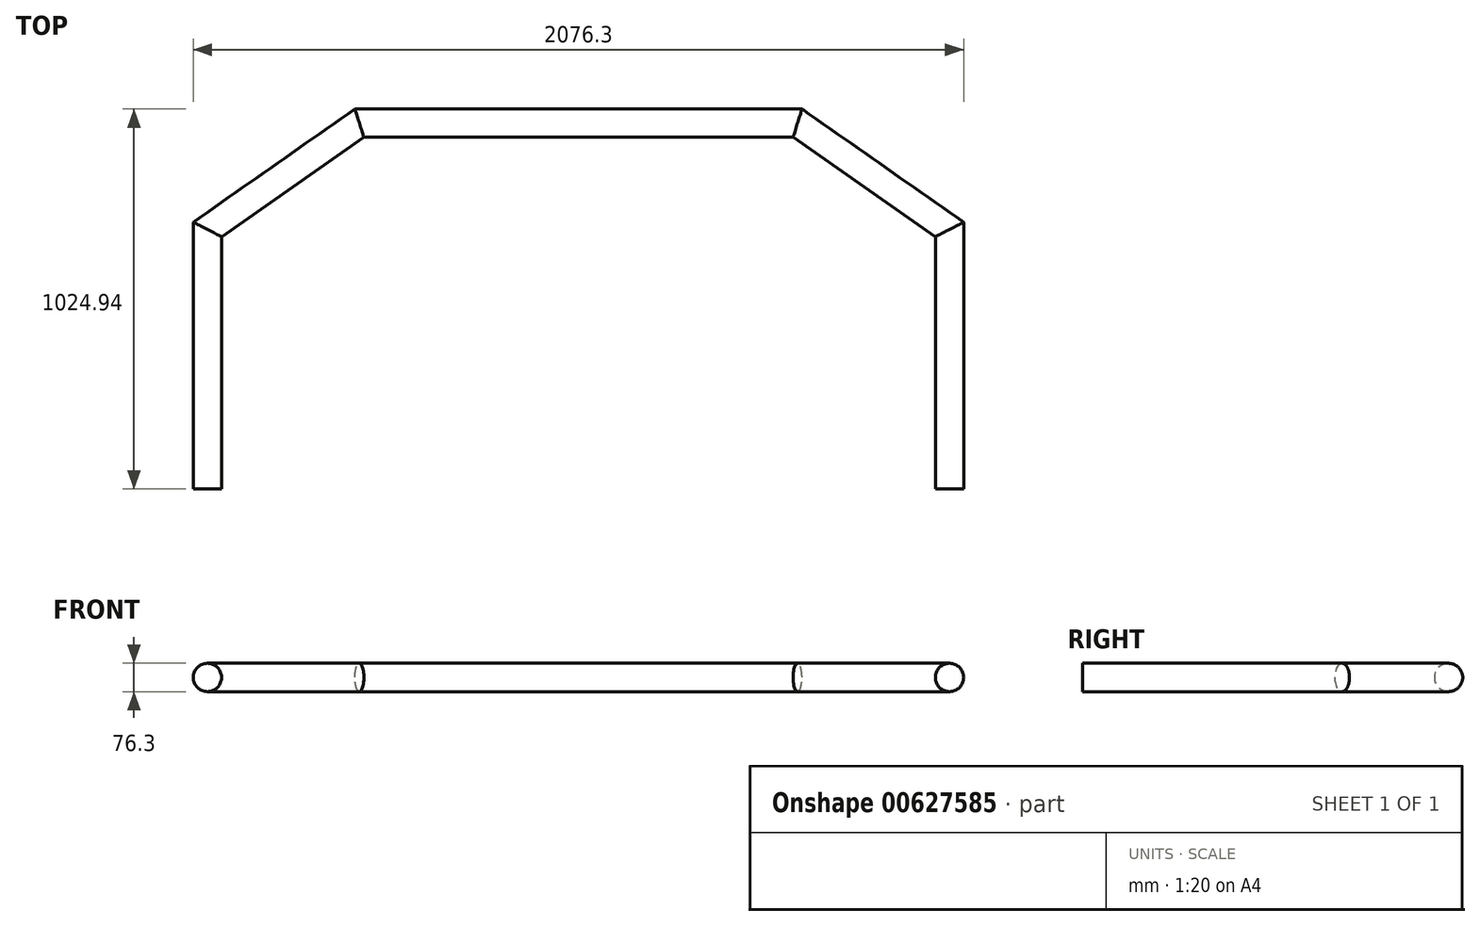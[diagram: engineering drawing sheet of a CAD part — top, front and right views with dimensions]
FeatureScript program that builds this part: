
annotation { "Feature Type Name" : "Feature", "Feature Type Description" : "" }
export const myFeature = defineFeature(function(context is Context, id is Id, definition is map)
    precondition{}
    {
        {
            var Q0;
            Q0=qCreatedBy(makeId("Top.planeOp"),FACE);
            var sketch = newSketch(context, id + "F0", { "sketchPlane" : qUnion([Q0])});
            skLineSegment(sketch, "E0", {"start": v(0, 0) * mm, "end": v(0, 700) * mm});
            skLineSegment(sketch, "E1", {"start": v(0, 700) * mm, "end": v(409.58, 986.79) * mm});
            skLineSegment(sketch, "E2", {"start": v(409.58, 986.79) * mm, "end": v(1590.42, 986.79) * mm});
            skLineSegment(sketch, "E3", {"start": v(1590.42, 986.79) * mm, "end": v(2000, 700) * mm});
            skLineSegment(sketch, "E4", {"start": v(2000, 700) * mm, "end": v(2000, 0) * mm});
            skSolve(sketch);
        }
        {
            var Q0;
            Q0=qCreatedBy(makeId("Front.planeOp"),FACE);
            var sketch = newSketch(context, id + "F1", { "sketchPlane" : qUnion([Q0])});
            skCircle(sketch, "E5", {"center": v(0, 0) * mm, "radius": 38.15 * mm});
            skSolve(sketch);
        }
        {
            var Q0;
            Q0=makeQuery(id+"F1.imprint","IMPRINT",FACE,{"disambiguationData":[TD([[makeQuery(id+"F1.imprint","IMPRINT",EDGE,{"derivedFrom":sQuery(id+"F1.wireOp",EDGE,"E5")}),1.0]])]});
            var Q1;
            Q1=sQuery(id+"F0.wireOp",EDGE,"E0");
            var Q2;
            Q2=sQuery(id+"F0.wireOp",EDGE,"E1");
            var Q3;
            Q3=sQuery(id+"F0.wireOp",EDGE,"E2");
            var Q4;
            Q4=sQuery(id+"F0.wireOp",EDGE,"E3");
            var Q5;
            Q5=sQuery(id+"F0.wireOp",EDGE,"E4");
            sweep(context, id + "F2", {"profiles" : qUnion([Q0]), "path" : qUnion([Q1, Q2, Q3, Q4, Q5])});
        }
    });
